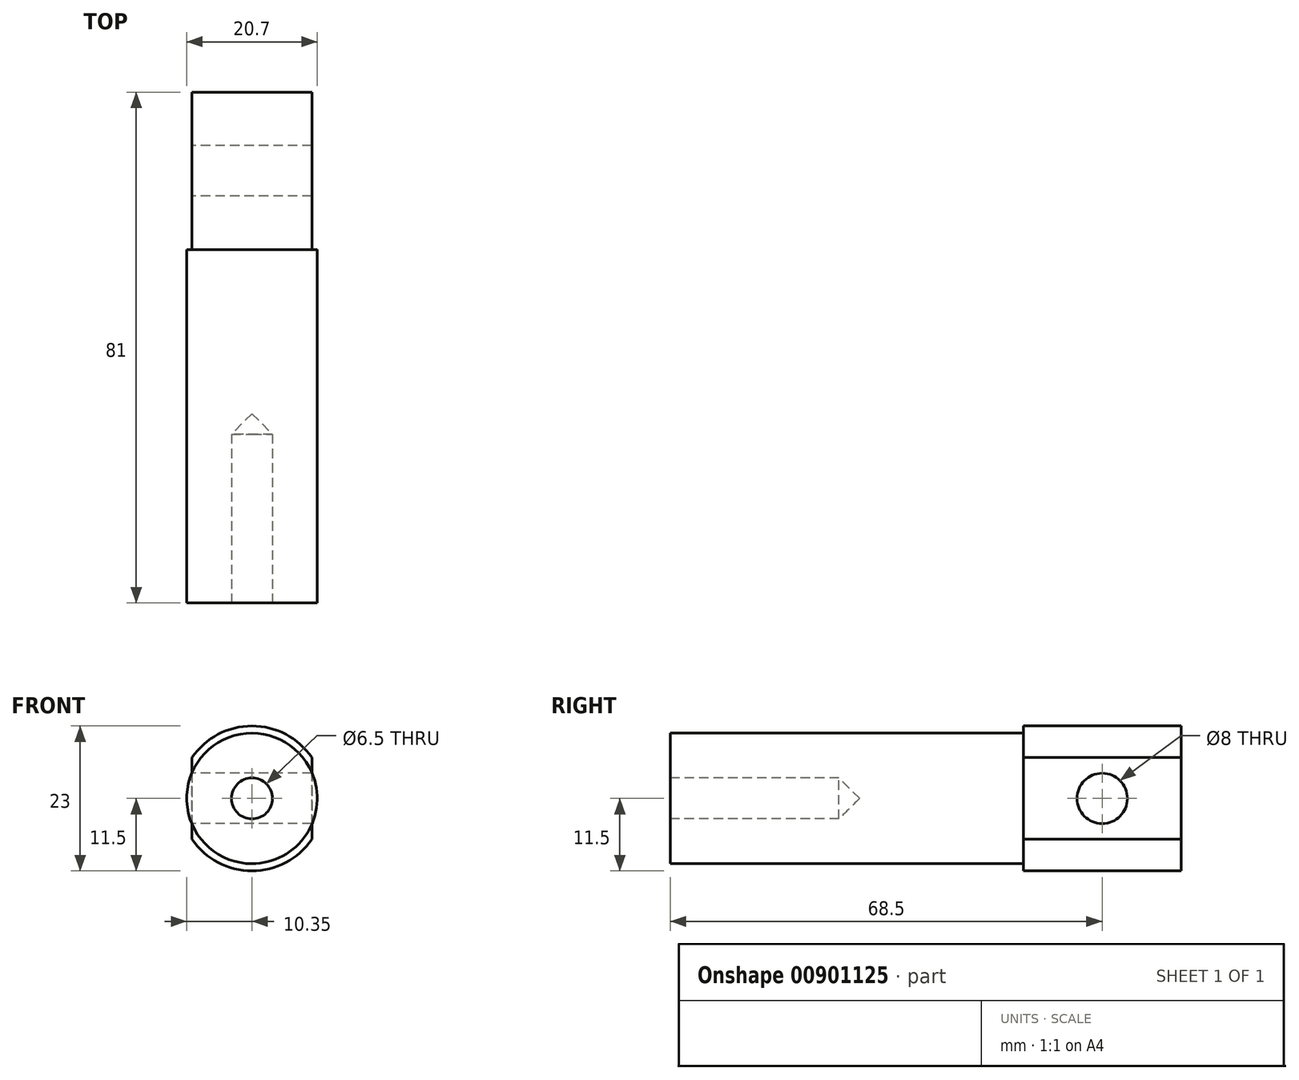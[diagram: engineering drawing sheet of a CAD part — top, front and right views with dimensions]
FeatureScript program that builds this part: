
annotation { "Feature Type Name" : "Feature", "Feature Type Description" : "" }
export const myFeature = defineFeature(function(context is Context, id is Id, definition is map)
    precondition{}
    {
        {
            var Q0;
            Q0=qCreatedBy(makeId("Front.planeOp"),FACE);
            var sketch = newSketch(context, id + "F0", { "sketchPlane" : qUnion([Q0])});
            skCircle(sketch, "E0", {"center": v(0, 0) * mm, "radius": 10.35 * mm});
            skSolve(sketch);
        }
        {
            var Q0;
            Q0=makeQuery(id+"F0.imprint","IMPRINT",FACE,{"disambiguationData":[TD([[makeQuery(id+"F0.imprint","IMPRINT",EDGE,{"derivedFrom":sQuery(id+"F0.wireOp",EDGE,"E0")}),1.0]])]});
            extrude(context, id + "F1", {"entities" : qUnion([Q0]), "depth" : 56 * mm, "offsetDistance" : 25 * mm});
        }
        {
            var Q0;
            Q0=makeQuery(id+"F1.opExtrude","CAP_FACE",FACE,{"disambiguationData":[OSD([sQuery(id+"F0.wireOp",EDGE,"E0")])],"isStart":true});
            var sketch = newSketch(context, id + "F2", { "sketchPlane" : qUnion([Q0])});
            skCircle(sketch, "E1", {"center": v(0, 0) * mm, "radius": 11.5 * mm});
            skSolve(sketch);
        }
        {
            var Q0;
            Q0 = qSketchRegion(id + "F2", true);
            extrude(context, id + "F3", {"entities" : qUnion([Q0]), "operationType" : NewBodyOperationType.ADD, "depth" : 25 * mm, "offsetDistance" : 25 * mm});
        }
        {
            var Q0;
            Q0=makeQuery(id+"F3.opExtrude","CAP_FACE",FACE,{"disambiguationData":[OSD([sQuery(id+"F2.wireOp",EDGE,"E1")])],"isStart":false});
            var sketch = newSketch(context, id + "F4", { "sketchPlane" : qUnion([Q0])});
            skLineSegment(sketch, "E2.bottom", {"start": v(9.5, 17.08) * mm, "end": v(-9.5, 17.08) * mm});
            skLineSegment(sketch, "E2.top", {"start": v(9.5, -17.08) * mm, "end": v(-9.5, -17.08) * mm});
            skLineSegment(sketch, "E2.left", {"start": v(9.5, 17.08) * mm, "end": v(9.5, -17.08) * mm});
            skLineSegment(sketch, "E2.right", {"start": v(-9.5, 17.08) * mm, "end": v(-9.5, -17.08) * mm});
            skPoint(sketch, "E2.middle", {"position": v(0, 0) * mm});
            skLineSegment(sketch, "E3.bottom", {"start": v(15.26, 24.53) * mm, "end": v(-15.26, 24.53) * mm});
            skLineSegment(sketch, "E3.top", {"start": v(15.26, -24.53) * mm, "end": v(-15.26, -24.53) * mm});
            skLineSegment(sketch, "E3.left", {"start": v(15.26, 24.53) * mm, "end": v(15.26, -24.53) * mm});
            skLineSegment(sketch, "E3.right", {"start": v(-15.26, 24.53) * mm, "end": v(-15.26, -24.53) * mm});
            skSolve(sketch);
        }
        {
            var Q0;
            {var subQ0=sQuery(id+"F4.wireOp",EDGE,"E2.right");var subQ1=makeQuery(id+"F3.opExtrude","CAP_EDGE",EDGE,{"disambiguationData":[OSD([sQuery(id+"F2.wireOp",EDGE,"E1")])],"isStart":false});var subQ2=makeQuery(id+"F4.imprint","INTERSECT",VERTEX,{"disambiguationData":[OD(0.0)],"derivedFrom":[subQ1,subQ0]});Q0=makeQuery(id+"F4.imprint","IMPRINT",FACE,{"disambiguationData":[TD([[makeQuery(id+"F4.imprint","IMPRINT",EDGE,{"disambiguationData":[TD([[subQ2,-1.0]])],"derivedFrom":subQ0}),-1.0]])]});}
            var Q1;
            {var subQ0=sQuery(id+"F4.wireOp",EDGE,"E2.left");var subQ1=makeQuery(id+"F3.opExtrude","CAP_EDGE",EDGE,{"disambiguationData":[OSD([sQuery(id+"F2.wireOp",EDGE,"E1")])],"isStart":false});var subQ2=makeQuery(id+"F4.imprint","INTERSECT",VERTEX,{"disambiguationData":[OD(0.0)],"derivedFrom":[subQ1,subQ0]});Q1=makeQuery(id+"F4.imprint","IMPRINT",FACE,{"disambiguationData":[TD([[makeQuery(id+"F4.imprint","IMPRINT",EDGE,{"disambiguationData":[TD([[subQ2,-1.0]])],"derivedFrom":subQ0}),1.0]])]});}
            var Q2;
            Q2=makeQuery(id+"F3.opExtrude","CAP_FACE",FACE,{"disambiguationData":[OSD([sQuery(id+"F2.wireOp",EDGE,"E1")])],"isStart":true});
            extrude(context, id + "F5", {"entities" : qUnion([Q0, Q1]), "operationType" : NewBodyOperationType.REMOVE, "endBound" : BoundingType.UP_TO_SURFACE, "oppositeDirection" : true, "depth" : 25 * mm, "endBoundEntityFace" : qUnion([Q2]), "offsetDistance" : 25 * mm});
        }
        {
            var Q0;
            Q0=makeQuery(id+"F5.boolean.opBoolean","COPY",FACE,{"derivedFrom":makeQuery(id+"F5.opExtrude","SWEPT_FACE",FACE,{"disambiguationData":[OSD([sQuery(id+"F4.wireOp",EDGE,"E2.left")])]})});
            var sketch = newSketch(context, id + "F6", { "sketchPlane" : qUnion([Q0])});
            skLineSegment(sketch, "E4", {"start": v(0, 6.48) * mm, "end": v(-25, -6.48) * mm, "construction": true});
            skCircle(sketch, "E5", {"center": v(-12.5, 0) * mm, "radius": 4 * mm});
            skSolve(sketch);
        }
        {
            var Q0;
            Q0 = qSketchRegion(id + "F6", true);
            extrude(context, id + "F7", {"entities" : qUnion([Q0]), "operationType" : NewBodyOperationType.REMOVE, "oppositeDirection" : true, "depth" : 25 * mm, "offsetDistance" : 25 * mm});
        }
        {
            var Q0;
            Q0=makeQuery(id+"F1.opExtrude","CAP_FACE",FACE,{"disambiguationData":[OSD([sQuery(id+"F0.wireOp",EDGE,"E0")])],"isStart":false});
            var sketch = newSketch(context, id + "F8", { "sketchPlane" : qUnion([Q0])});
            skCircle(sketch, "E6", {"center": v(0, 0) * mm, "radius": 3.25 * mm});
            skSolve(sketch);
        }
        {
            var Q0;
            Q0 = qSketchRegion(id + "F8", true);
            extrude(context, id + "F9", {"entities" : qUnion([Q0]), "operationType" : NewBodyOperationType.REMOVE, "oppositeDirection" : true, "depth" : 30 * mm, "offsetDistance" : 25 * mm});
        }
        {
            var Q0;
            Q0=makeQuery(id+"F9.boolean.opBoolean","COPY",EDGE,{"derivedFrom":makeQuery(id+"F9.opExtrude","CAP_EDGE",EDGE,{"disambiguationData":[OSD([sQuery(id+"F8.wireOp",EDGE,"E6")])],"isStart":false})});
            chamfer(context, id + "F10", {"entities" : qUnion([Q0]), "width" : (6.5 / 2) * mm, "tangentPropagation" : true});
        }
    });
